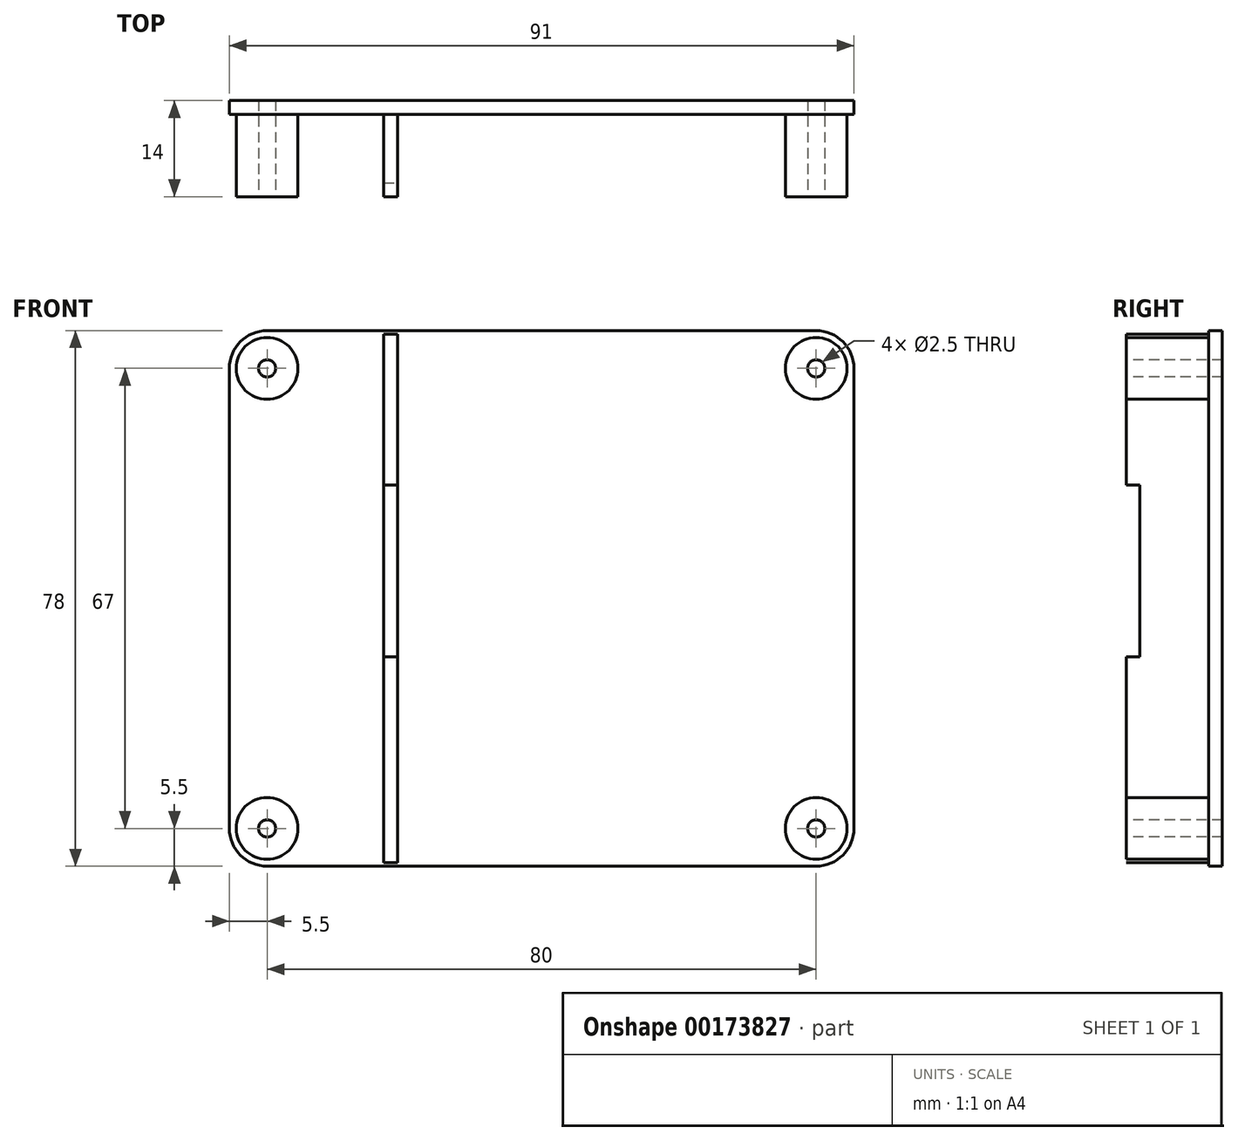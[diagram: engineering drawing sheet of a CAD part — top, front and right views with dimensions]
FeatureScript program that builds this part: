
annotation { "Feature Type Name" : "Feature", "Feature Type Description" : "" }
export const myFeature = defineFeature(function(context is Context, id is Id, definition is map)
    precondition{}
    {
        {
            var Q0;
            Q0=qCreatedBy(makeId("Front.planeOp"),FACE);
            var sketch = newSketch(context, id + "F0", { "sketchPlane" : qUnion([Q0])});
            skLineSegment(sketch, "E0.bottom", {"start": v(-17, 77.5) * mm, "end": v(63, 77.5) * mm});
            skLineSegment(sketch, "E0.top", {"start": v(-17, -0.5) * mm, "end": v(63, -0.5) * mm});
            skLineSegment(sketch, "E0.left", {"start": v(-22.5, 72) * mm, "end": v(-22.5, 5) * mm});
            skLineSegment(sketch, "E0.right", {"start": v(68.5, 72) * mm, "end": v(68.5, 5) * mm});
            skPoint(sketch, "E1.visualSharp", {"position": v(68.5, 77.5) * mm});
            skArc(sketch, "E1.filletArc", {"start": v(68.5, 72) * mm, "mid": v(66.89, 75.89) * mm, "end": v(63, 77.5) * mm});
            skPoint(sketch, "E2.visualSharp", {"position": v(-22.5, 77.5) * mm});
            skArc(sketch, "E2.filletArc", {"start": v(-17, 77.5) * mm, "mid": v(-20.89, 75.89) * mm, "end": v(-22.5, 72) * mm});
            skPoint(sketch, "E3.visualSharp", {"position": v(-22.5, -0.5) * mm});
            skArc(sketch, "E3.filletArc", {"start": v(-22.5, 5) * mm, "mid": v(-20.89, 1.11) * mm, "end": v(-17, -0.5) * mm});
            skPoint(sketch, "E4.visualSharp", {"position": v(68.5, -0.5) * mm});
            skArc(sketch, "E4.filletArc", {"start": v(63, -0.5) * mm, "mid": v(66.89, 1.11) * mm, "end": v(68.5, 5) * mm});
            skCircle(sketch, "E5", {"center": v(63, 72) * mm, "radius": 4.5 * mm, "construction": true});
            skCircle(sketch, "E6", {"center": v(63, 5) * mm, "radius": 4.5 * mm, "construction": true});
            skCircle(sketch, "E7", {"center": v(-17, 5) * mm, "radius": 4.5 * mm, "construction": true});
            skCircle(sketch, "E8", {"center": v(-17, 72) * mm, "radius": 4.5 * mm, "construction": true});
            skSolve(sketch);
        }
        {
            var Q0;
            Q0 = qSketchRegion(id + "F0", true);
            extrude(context, id + "F1", {"entities" : qUnion([Q0]), "oppositeDirection" : true, "depth" : 2 * mm, "offsetDistance" : 25 * mm});
        }
        {
            var Q0;
            Q0=qCreatedBy(makeId("Front.planeOp"),FACE);
            var sketch = newSketch(context, id + "F2", { "sketchPlane" : qUnion([Q0])});
            skCircle(sketch, "E9.0", {"center": v(-17, 72) * mm, "radius": 4.5 * mm});
            skCircle(sketch, "E10.0", {"center": v(63, 72) * mm, "radius": 4.5 * mm});
            skCircle(sketch, "E11.0", {"center": v(-17, 5) * mm, "radius": 4.5 * mm});
            skCircle(sketch, "E12.0", {"center": v(63, 5) * mm, "radius": 4.5 * mm});
            skLineSegment(sketch, "E13", {"start": v(0, 0) * mm, "end": v(0, 77) * mm});
            skPoint(sketch, "E14.orphan", {"position": v(63, 77.5) * mm});
            skPoint(sketch, "E15.orphan", {"position": v(-17, 77.5) * mm});
            skPoint(sketch, "E16.orphan", {"position": v(-17, -0.5) * mm});
            skPoint(sketch, "E17.orphan", {"position": v(63, -0.5) * mm});
            skLineSegment(sketch, "E18.0", {"start": v(2, 0) * mm, "end": v(2, 77) * mm});
            skLineSegment(sketch, "E19", {"start": v(0, 0) * mm, "end": v(2, 0) * mm});
            skLineSegment(sketch, "E20", {"start": v(0, 77) * mm, "end": v(2, 77) * mm});
            skSolve(sketch);
        }
        {
            var Q0;
            Q0 = qSketchRegion(id + "F2", true);
            extrude(context, id + "F3", {"entities" : qUnion([Q0]), "operationType" : NewBodyOperationType.ADD, "depth" : 12 * mm, "offsetDistance" : 25 * mm});
        }
        {
            var Q0;
            Q0=makeQuery(id+"F3.opExtrude","CAP_FACE",FACE,{"disambiguationData":[OSD([sQuery(id+"F2.wireOp",EDGE,"E9.0")])],"isStart":false});
            var sketch = newSketch(context, id + "F4", { "sketchPlane" : qUnion([Q0])});
            skCircle(sketch, "E21.0", {"center": v(-17, 72) * mm, "radius": 4.5 * mm});
            skCircle(sketch, "E22.0", {"center": v(63, 72) * mm, "radius": 4.5 * mm});
            skCircle(sketch, "E23.0", {"center": v(-17, 5) * mm, "radius": 4.5 * mm});
            skCircle(sketch, "E24.0", {"center": v(63, 5) * mm, "radius": 4.5 * mm});
            skCircle(sketch, "E25", {"center": v(-17, 72) * mm, "radius": 1.25 * mm});
            skCircle(sketch, "E26", {"center": v(-17, 5) * mm, "radius": 1.25 * mm});
            skCircle(sketch, "E27", {"center": v(63, 5) * mm, "radius": 1.25 * mm});
            skCircle(sketch, "E28", {"center": v(63, 72) * mm, "radius": 1.25 * mm});
            skSolve(sketch);
        }
        {
            var Q0;
            Q0=makeQuery(id+"F4.imprint","IMPRINT",FACE,{"disambiguationData":[TD([[makeQuery(id+"F4.imprint","IMPRINT",EDGE,{"derivedFrom":sQuery(id+"F4.wireOp",EDGE,"E25")}),1.0]])]});
            var Q1;
            Q1=makeQuery(id+"F4.imprint","IMPRINT",FACE,{"disambiguationData":[TD([[makeQuery(id+"F4.imprint","IMPRINT",EDGE,{"derivedFrom":sQuery(id+"F4.wireOp",EDGE,"E28")}),1.0]])]});
            var Q2;
            Q2=makeQuery(id+"F4.imprint","IMPRINT",FACE,{"disambiguationData":[TD([[makeQuery(id+"F4.imprint","IMPRINT",EDGE,{"derivedFrom":sQuery(id+"F4.wireOp",EDGE,"E27")}),1.0]])]});
            var Q3;
            Q3=makeQuery(id+"F4.imprint","IMPRINT",FACE,{"disambiguationData":[TD([[makeQuery(id+"F4.imprint","IMPRINT",EDGE,{"derivedFrom":sQuery(id+"F4.wireOp",EDGE,"E26")}),1.0]])]});
            extrude(context, id + "F5", {"entities" : qUnion([Q0, Q1, Q2, Q3]), "operationType" : NewBodyOperationType.REMOVE, "oppositeDirection" : true, "depth" : 25 * mm, "offsetDistance" : 25 * mm});
        }
        {
            var Q0;
            Q0=makeQuery(id+"F3.opExtrude","CAP_FACE",FACE,{"disambiguationData":[OSD([sQuery(id+"F2.wireOp",EDGE,"E13"),sQuery(id+"F2.wireOp",EDGE,"E18.0"),sQuery(id+"F2.wireOp",EDGE,"E19"),sQuery(id+"F2.wireOp",EDGE,"E20")])],"isStart":false});
            var sketch = newSketch(context, id + "F6", { "sketchPlane" : qUnion([Q0])});
            skLineSegment(sketch, "E29.bottom", {"start": v(0, 55) * mm, "end": v(2, 55) * mm});
            skLineSegment(sketch, "E29.top", {"start": v(0, 30) * mm, "end": v(2, 30) * mm});
            skLineSegment(sketch, "E29.left", {"start": v(0, 55) * mm, "end": v(0, 30) * mm});
            skLineSegment(sketch, "E29.right", {"start": v(2, 55) * mm, "end": v(2, 30) * mm});
            skSolve(sketch);
        }
        {
            var Q0;
            Q0 = qSketchRegion(id + "F6", true);
            extrude(context, id + "F7", {"entities" : qUnion([Q0]), "operationType" : NewBodyOperationType.REMOVE, "oppositeDirection" : true, "depth" : 2 * mm, "offsetDistance" : 25 * mm});
        }
    });
